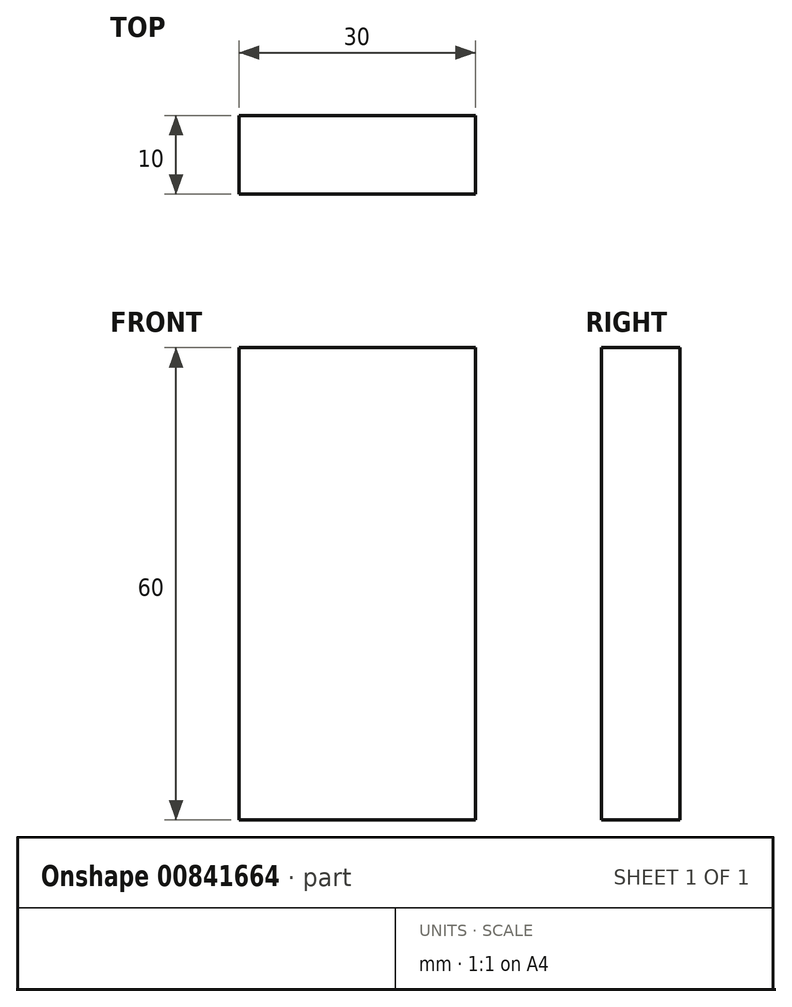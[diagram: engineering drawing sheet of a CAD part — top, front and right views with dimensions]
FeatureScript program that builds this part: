
annotation { "Feature Type Name" : "Feature", "Feature Type Description" : "" }
export const myFeature = defineFeature(function(context is Context, id is Id, definition is map)
    precondition{}
    {
        {
            var Q0;
            Q0=qCreatedBy(makeId("Front.planeOp"),FACE);
            var sketch = newSketch(context, id + "F0", { "sketchPlane" : qUnion([Q0])});
            skLineSegment(sketch, "E0", {"start": v(-15.78, 0) * mm, "end": v(-15.78, 60) * mm});
            skLineSegment(sketch, "E1", {"start": v(-15.78, 60) * mm, "end": v(14.22, 60) * mm});
            skLineSegment(sketch, "E2", {"start": v(14.22, 60) * mm, "end": v(14.22, 0) * mm});
            skLineSegment(sketch, "E3", {"start": v(-15.78, 0) * mm, "end": v(14.22, 0) * mm});
            skSolve(sketch);
        }
        {
            var Q0;
            Q0=makeQuery(id+"F0.imprint","IMPRINT",FACE,{"disambiguationData":[TD([[makeQuery(id+"F0.imprint","IMPRINT",EDGE,{"derivedFrom":sQuery(id+"F0.wireOp",EDGE,"E0")}),-1.0]])]});
            extrude(context, id + "F1", {"entities" : qUnion([Q0]), "depth" : 10 * mm, "offsetDistance" : 25 * mm});
        }
    });
